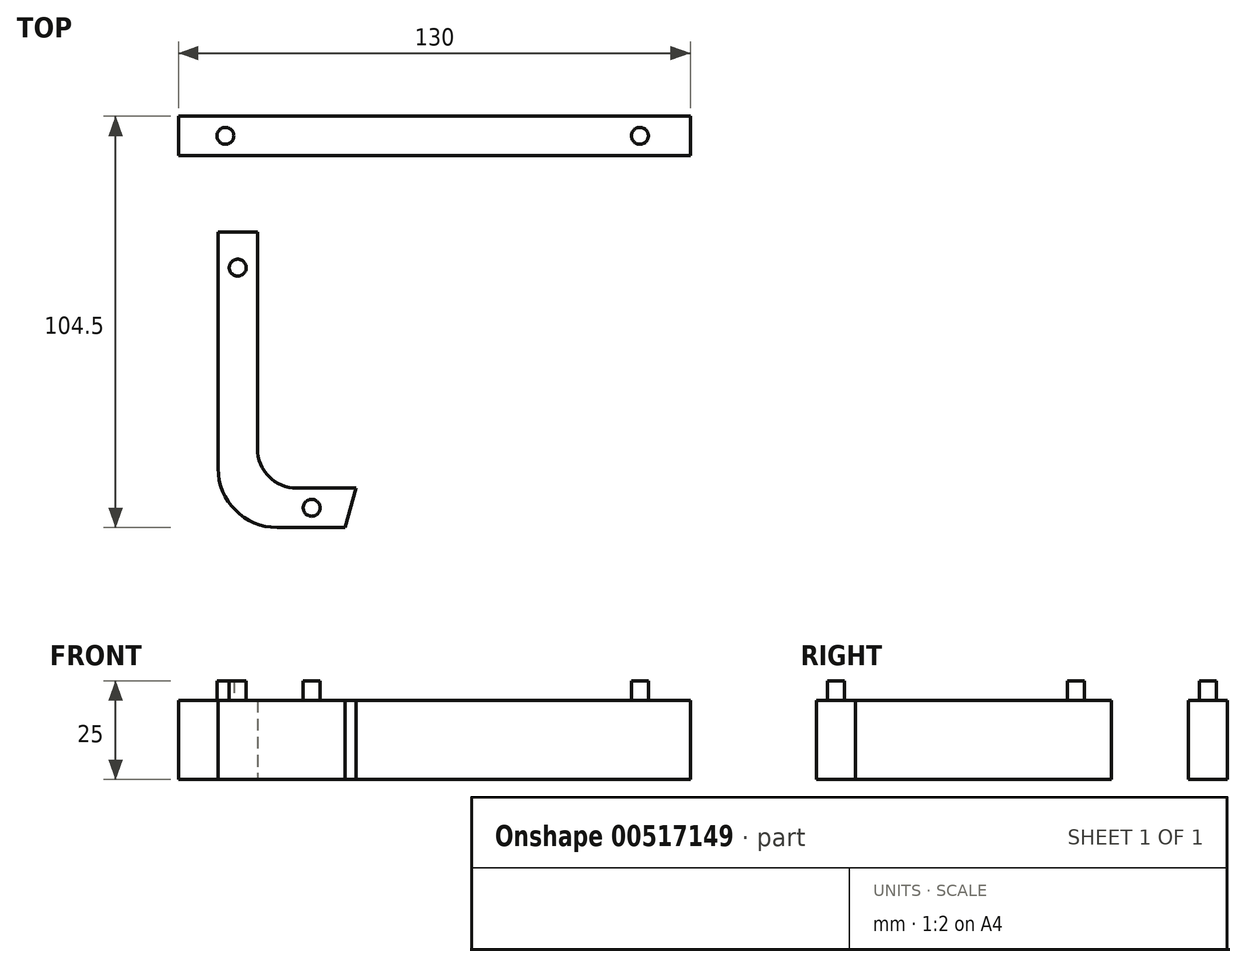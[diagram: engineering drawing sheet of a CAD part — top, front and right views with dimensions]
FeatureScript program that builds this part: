
annotation { "Feature Type Name" : "Feature", "Feature Type Description" : "" }
export const myFeature = defineFeature(function(context is Context, id is Id, definition is map)
    precondition{}
    {
        {
            var Q0;
            Q0=qCreatedBy(makeId("Top.planeOp"),FACE);
            var sketch = newSketch(context, id + "F0", { "sketchPlane" : qUnion([Q0])});
            skLineSegment(sketch, "E0", {"start": v(-62.5, 34.88) * mm, "end": v(67.5, 34.88) * mm});
            skLineSegment(sketch, "E1", {"start": v(-62.5, 34.88) * mm, "end": v(-62.5, 24.88) * mm});
            skLineSegment(sketch, "E2", {"start": v(-62.5, 24.88) * mm, "end": v(67.5, 24.88) * mm});
            skLineSegment(sketch, "E3", {"start": v(67.5, 34.88) * mm, "end": v(67.5, 24.88) * mm});
            skLineSegment(sketch, "E4", {"start": v(-42.47, 5.38) * mm, "end": v(-42.47, -49.62) * mm});
            skLineSegment(sketch, "E5", {"start": v(-32.47, -59.62) * mm, "end": v(-17.47, -59.62) * mm});
            skLineSegment(sketch, "E6", {"start": v(-42.47, 5.38) * mm, "end": v(-52.47, 5.38) * mm});
            skLineSegment(sketch, "E7", {"start": v(-17.47, -69.62) * mm, "end": v(-37.47, -69.62) * mm});
            skLineSegment(sketch, "E8", {"start": v(-52.47, -54.62) * mm, "end": v(-52.47, 5.38) * mm});
            skPoint(sketch, "E9.visualSharp", {"position": v(-42.47, -59.62) * mm});
            skArc(sketch, "E9.filletArc", {"start": v(-42.47, -49.62) * mm, "mid": v(-39.54, -56.69) * mm, "end": v(-32.47, -59.62) * mm});
            skPoint(sketch, "E10.visualSharp", {"position": v(-52.47, -69.62) * mm});
            skArc(sketch, "E10.filletArc", {"start": v(-52.47, -54.62) * mm, "mid": v(-48.08, -65.22) * mm, "end": v(-37.47, -69.62) * mm});
            skLineSegment(sketch, "E11", {"start": v(-17.47, -59.62) * mm, "end": v(-20.24, -69.62) * mm});
            skLineSegment(sketch, "E12", {"start": v(67.5, 29.88) * mm, "end": v(67.5, 34.88) * mm});
            skLineSegment(sketch, "E13", {"start": v(67.5, 34.88) * mm, "end": v(52.5, 34.88) * mm});
            skLineSegment(sketch, "E14", {"start": v(52.5, 34.88) * mm, "end": v(67.5, 34.88) * mm});
            skLineSegment(sketch, "E15", {"start": v(-62.5, 34.88) * mm, "end": v(-47.5, 34.88) * mm});
            skLineSegment(sketch, "E16", {"start": v(-47.5, 34.88) * mm, "end": v(-62.5, 34.88) * mm});
            skSolve(sketch);
        }
        {
            var Q0;
            Q0=makeQuery(id+"F0.imprint","IMPRINT",FACE,{"disambiguationData":[TD([[makeQuery(id+"F0.imprint","IMPRINT",EDGE,{"derivedFrom":sQuery(id+"F0.wireOp",EDGE,"E0")}),-1.0]])]});
            extrude(context, id + "F1", {"entities" : qUnion([Q0]), "depth" : 20 * mm, "offsetDistance" : 25 * mm});
        }
        {
            var Q0;
            Q0=makeQuery(id+"F0.imprint","IMPRINT",FACE,{"disambiguationData":[TD([[makeQuery(id+"F0.imprint","IMPRINT",EDGE,{"derivedFrom":sQuery(id+"F0.wireOp",EDGE,"E4")}),-1.0]])]});
            extrude(context, id + "F2", {"entities" : qUnion([Q0]), "depth" : 20 * mm, "offsetDistance" : 25 * mm});
        }
        {
            var Q0;
            Q0=makeQuery(id+"F1.opExtrude","CAP_FACE",FACE,{"disambiguationData":[OSD([sQuery(id+"F0.wireOp",EDGE,"E0"),sQuery(id+"F0.wireOp",EDGE,"E1"),sQuery(id+"F0.wireOp",EDGE,"E2"),sQuery(id+"F0.wireOp",EDGE,"E3"),sQuery(id+"F0.wireOp",EDGE,"E12"),sQuery(id+"F0.wireOp",EDGE,"E14"),sQuery(id+"F0.wireOp",EDGE,"E16")])],"isStart":false});
            var sketch = newSketch(context, id + "F3", { "sketchPlane" : qUnion([Q0])});
            skCircle(sketch, "E17", {"center": v(-50.61, 29.88) * mm, "radius": 2.15 * mm});
            skCircle(sketch, "E18", {"center": v(54.7, 29.88) * mm, "radius": 2.15 * mm});
            skSolve(sketch);
        }
        {
            var Q0;
            Q0=makeQuery(id+"F3.imprint","IMPRINT",FACE,{"disambiguationData":[TD([[makeQuery(id+"F3.imprint","IMPRINT",EDGE,{"derivedFrom":sQuery(id+"F3.wireOp",EDGE,"E17")}),1.0]])]});
            var Q1;
            Q1=makeQuery(id+"F3.imprint","IMPRINT",FACE,{"disambiguationData":[TD([[makeQuery(id+"F3.imprint","IMPRINT",EDGE,{"derivedFrom":sQuery(id+"F3.wireOp",EDGE,"E18")}),1.0]])]});
            extrude(context, id + "F4", {"entities" : qUnion([Q0, Q1]), "operationType" : NewBodyOperationType.ADD, "depth" : 5 * mm, "offsetDistance" : 25 * mm});
        }
        {
            var Q0;
            Q0=makeQuery(id+"F2.opExtrude","CAP_FACE",FACE,{"disambiguationData":[OSD([sQuery(id+"F0.wireOp",EDGE,"E4"),sQuery(id+"F0.wireOp",EDGE,"E5"),sQuery(id+"F0.wireOp",EDGE,"E6"),sQuery(id+"F0.wireOp",EDGE,"E7"),sQuery(id+"F0.wireOp",EDGE,"E8"),sQuery(id+"F0.wireOp",EDGE,"E9.filletArc"),sQuery(id+"F0.wireOp",EDGE,"E10.filletArc"),sQuery(id+"F0.wireOp",EDGE,"E11")])],"isStart":false});
            var sketch = newSketch(context, id + "F5", { "sketchPlane" : qUnion([Q0])});
            skPoint(sketch, "E19.startSnap0", {"position": v(-47.47, 5.38) * mm});
            skCircle(sketch, "E20", {"center": v(-47.47, -3.62) * mm, "radius": 2.15 * mm});
            skCircle(sketch, "E21", {"center": v(-28.7, -64.62) * mm, "radius": 2.15 * mm});
            skSolve(sketch);
        }
        {
            var Q0;
            Q0=makeQuery(id+"F5.imprint","IMPRINT",FACE,{"disambiguationData":[TD([[makeQuery(id+"F5.imprint","IMPRINT",EDGE,{"derivedFrom":sQuery(id+"F5.wireOp",EDGE,"E20")}),1.0]])]});
            var Q1;
            Q1=makeQuery(id+"F5.imprint","IMPRINT",FACE,{"disambiguationData":[TD([[makeQuery(id+"F5.imprint","IMPRINT",EDGE,{"derivedFrom":sQuery(id+"F5.wireOp",EDGE,"E21")}),1.0]])]});
            extrude(context, id + "F6", {"entities" : qUnion([Q0, Q1]), "operationType" : NewBodyOperationType.ADD, "depth" : 5 * mm, "offsetDistance" : 25 * mm});
        }
    });
